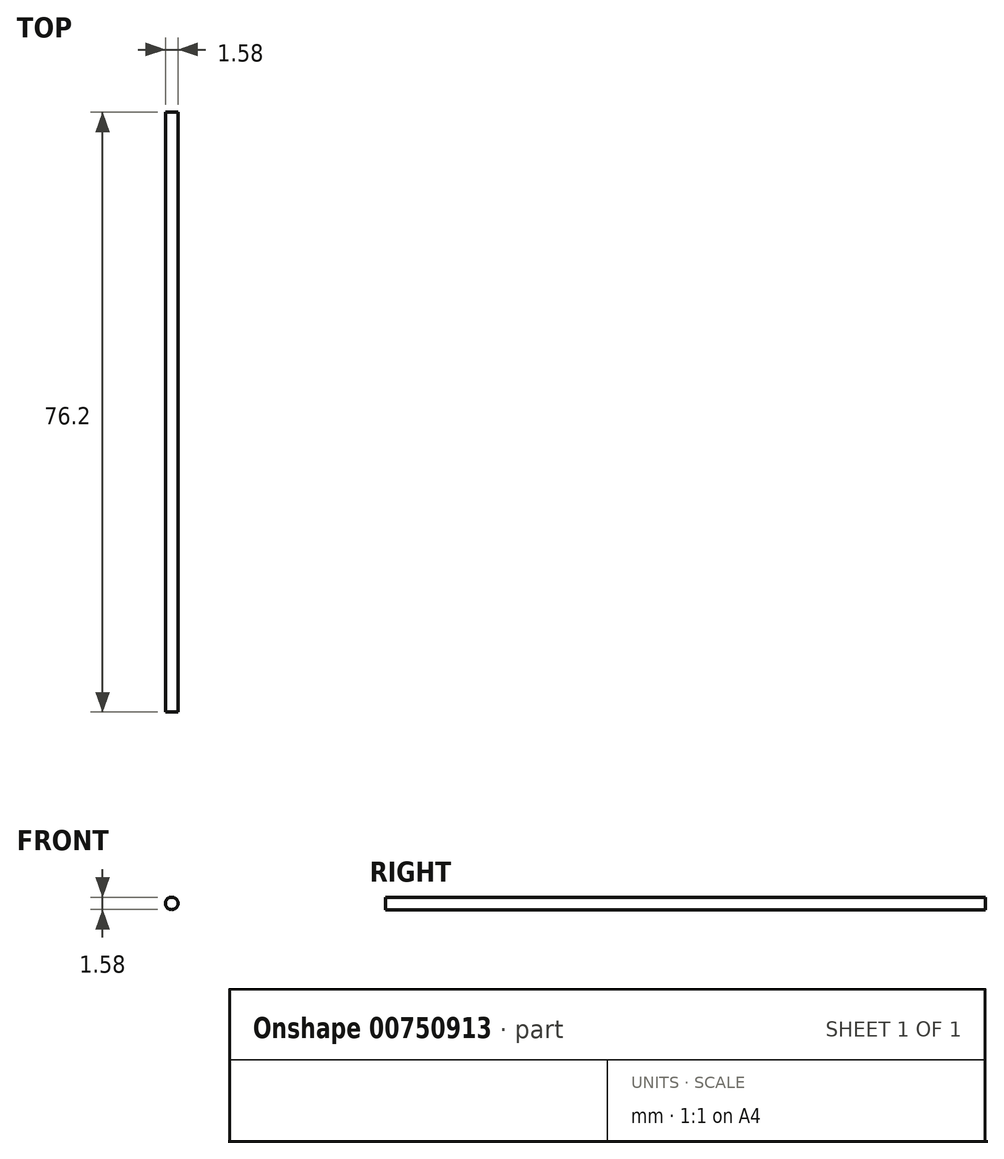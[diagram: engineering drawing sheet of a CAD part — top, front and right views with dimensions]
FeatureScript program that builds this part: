
annotation { "Feature Type Name" : "Feature", "Feature Type Description" : "" }
export const myFeature = defineFeature(function(context is Context, id is Id, definition is map)
    precondition{}
    {
        {
            var Q0;
            Q0=qCreatedBy(makeId("Front.planeOp"),FACE);
            var sketch = newSketch(context, id + "F0", { "sketchPlane" : qUnion([Q0])});
            skCircle(sketch, "E0", {"center": v(0, 0) * mm, "radius": 0.8 * mm});
            skSolve(sketch);
        }
        {
            var Q0;
            Q0 = qSketchRegion(id + "F0", true);
            extrude(context, id + "F1", {"entities" : qUnion([Q0]), "oppositeDirection" : true, "depth" : 76.2 * mm, "offsetDistance" : 25.4 * mm});
        }
    });
